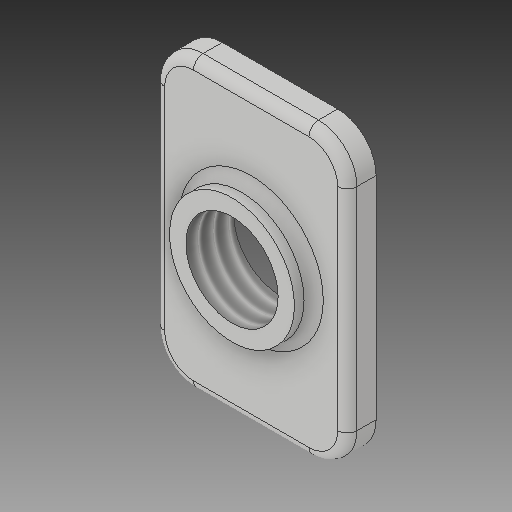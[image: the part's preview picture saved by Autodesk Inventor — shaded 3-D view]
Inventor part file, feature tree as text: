
AUTODESK INVENTOR PART (.ipt)
format: ipt  version: 2018 (Build 220112000, 112)  size: 164,352 bytes
history: native  units: mm
features: other x3, sketch x2
ambient origin geometry x8: Origin, YZ Plane, XZ Plane, XY Plane, X Axis, Y Axis, Z Axis, Center Point
bodies: Solid1 (feature_tree)
feature tree (5):
  other  "M5 Tee Nut_MIR.ipt"
  other  "Solid1::M5 Tee Nut_MIR.ipt"
  other  "TaggingFeature1"
  sketch  "Sketch1"  dims[d0=10.0mm]
  sketch  "Sketch2"
